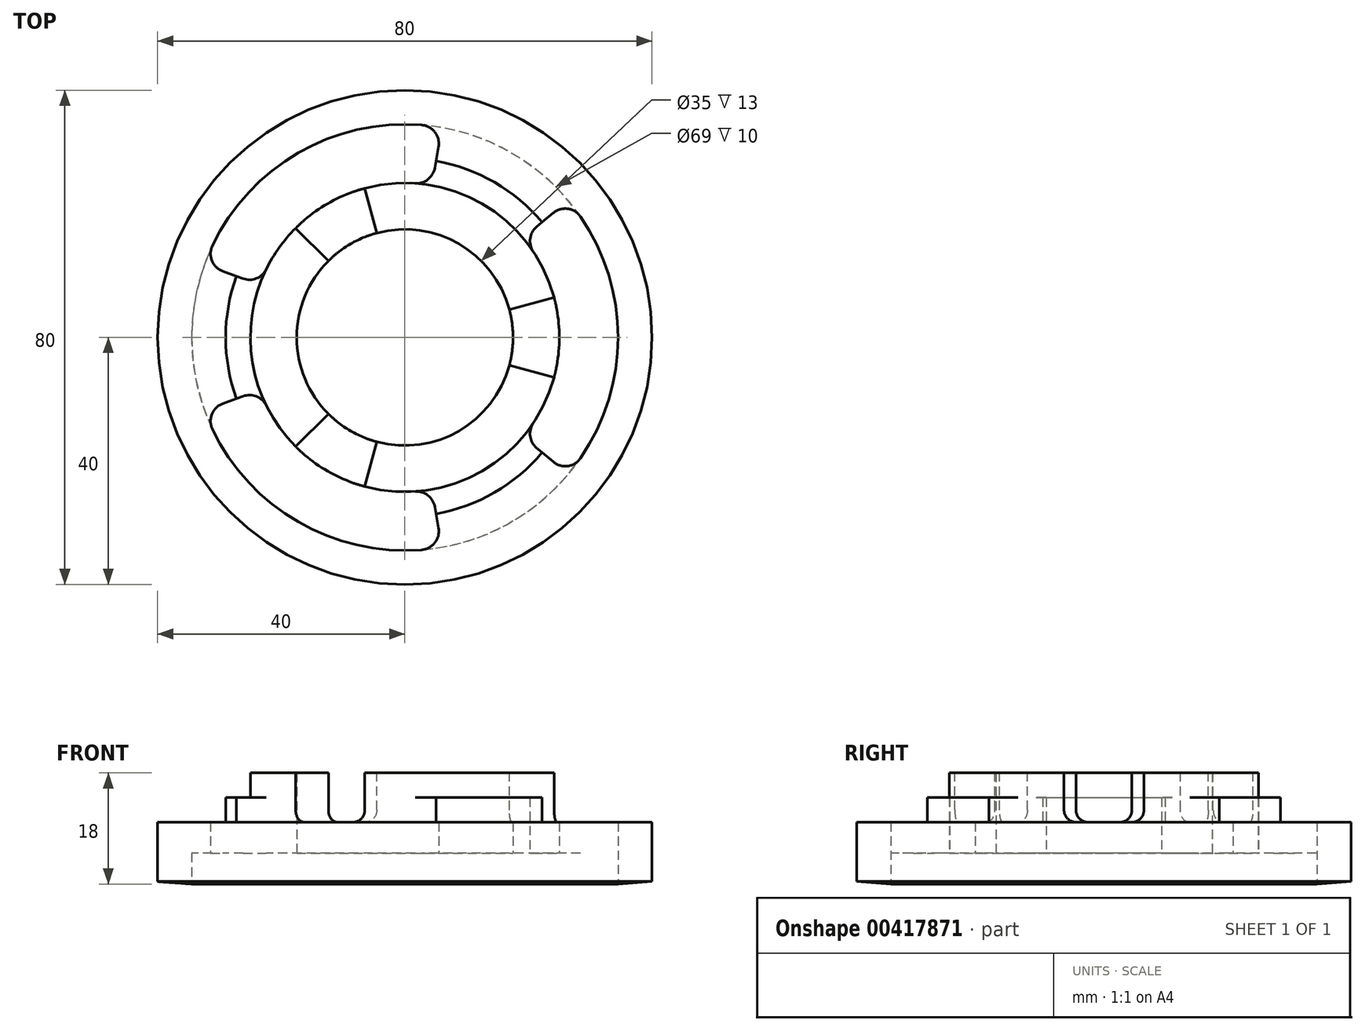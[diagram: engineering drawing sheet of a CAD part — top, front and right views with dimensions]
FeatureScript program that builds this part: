
annotation { "Feature Type Name" : "Feature", "Feature Type Description" : "" }
export const myFeature = defineFeature(function(context is Context, id is Id, definition is map)
    precondition{}
    {
        {
            var Q0;
            Q0=qCreatedBy(makeId("Front.planeOp"),FACE);
            var sketch = newSketch(context, id + "F0", { "sketchPlane" : qUnion([Q0])});
            skLineSegment(sketch, "E0.bottom", {"start": v(-34.5, 3) * mm, "end": v(34.5, 3) * mm});
            skLineSegment(sketch, "E0.left", {"start": v(-34.5, 3) * mm, "end": v(-34.5, -2) * mm});
            skLineSegment(sketch, "E0.right", {"start": v(34.5, 3) * mm, "end": v(34.5, -2) * mm});
            skLineSegment(sketch, "E1", {"start": v(62.5, 0) * mm, "end": v(34.5, -2) * mm});
            skPoint(sketch, "E2.orphan", {"position": v(34.5, 0) * mm});
            skLineSegment(sketch, "E3", {"start": v(-62.5, 0) * mm, "end": v(-34.5, -2) * mm});
            skPoint(sketch, "E4.orphan", {"position": v(0, 3) * mm});
            skLineSegment(sketch, "E5", {"start": v(-34.5, -2) * mm, "end": v(34.5, -2) * mm, "construction": true});
            skLineSegment(sketch, "E6", {"start": v(-40, -1.6) * mm, "end": v(-40, 8) * mm});
            skLineSegment(sketch, "E7", {"start": v(-40, 8) * mm, "end": v(-29, 8) * mm});
            skLineSegment(sketch, "E8", {"start": v(40, 8) * mm, "end": v(40, -1.6) * mm});
            skLineSegment(sketch, "E9", {"start": v(-29, 8) * mm, "end": v(-29, 12) * mm});
            skLineSegment(sketch, "E10", {"start": v(-25, 16) * mm, "end": v(25, 16) * mm});
            skLineSegment(sketch, "E11", {"start": v(29, 12) * mm, "end": v(29, 8) * mm});
            skLineSegment(sketch, "E12.trimOffspring", {"start": v(29, 8) * mm, "end": v(40, 8) * mm});
            skLineSegment(sketch, "E13", {"start": v(17.5, 16) * mm, "end": v(17.5, 3) * mm});
            skLineSegment(sketch, "E14", {"start": v(-17.5, 16) * mm, "end": v(-17.5, 3) * mm});
            skLineSegment(sketch, "E15", {"start": v(0, 0) * mm, "end": v(0, 16) * mm, "construction": true});
            skLineSegment(sketch, "E16", {"start": v(25, 16) * mm, "end": v(25, 12) * mm});
            skLineSegment(sketch, "E17", {"start": v(25, 12) * mm, "end": v(29, 12) * mm});
            skPoint(sketch, "E18.orphan", {"position": v(29, 16) * mm});
            skLineSegment(sketch, "E19.MirrorCS", {"start": v(-25, 12) * mm, "end": v(-29, 12) * mm});
            skLineSegment(sketch, "E20.MirrorCS", {"start": v(-25, 16) * mm, "end": v(-25, 12) * mm});
            skPoint(sketch, "E21.orphan", {"position": v(-29, 16) * mm});
            skSolve(sketch);
        }
        {
            var Q0;
            {var subQ1=sQuery(id+"F0.wireOp",EDGE,"E0.right");Q0=makeQuery(id+"F0.imprint","IMPRINT",FACE,{"disambiguationData":[TD([[makeQuery(id+"F0.imprint","IMPRINT",EDGE,{"derivedFrom":subQ1}),1.0]])]});}
            var Q1;
            {var subQ1=sQuery(id+"F0.wireOp",EDGE,"E11");Q1=makeQuery(id+"F0.imprint","IMPRINT",FACE,{"disambiguationData":[TD([[makeQuery(id+"F0.imprint","IMPRINT",EDGE,{"derivedFrom":subQ1}),-1.0]])]});}
            var Q2;
            Q2=sQuery(id+"F0.wireOp",EDGE,"E15");
            revolve(context, id + "F1", {"surfaceOperationType" : NewSurfaceOperationType.NEW, "entities" : qUnion([Q0, Q1]), "axis" : qUnion([Q2]), "revolveType" : RevolveType.FULL});
        }
        {
            var Q0;
            Q0=makeQuery(id+"F1.opRevolve","SWEPT_FACE",FACE,{"disambiguationData":[OSD([sQuery(id+"F0.wireOp",EDGE,"E0.bottom")])]});
            var sketch = newSketch(context, id + "F2", { "sketchPlane" : qUnion([Q0])});
            skArc(sketch, "E22.0", {"start": v(26.43, -22.18) * mm, "mid": v(34.5, 0) * mm, "end": v(26.43, 22.18) * mm});
            skArc(sketch, "E23", {"start": v(19.15, -16.07) * mm, "mid": v(25, 0) * mm, "end": v(19.15, 16.07) * mm});
            skLineSegment(sketch, "E24", {"start": v(19.15, 16.07) * mm, "end": v(26.43, 22.18) * mm});
            skLineSegment(sketch, "E25", {"start": v(26.43, 22.18) * mm, "end": v(19.15, 16.07) * mm});
            skLineSegment(sketch, "E26", {"start": v(26.43, -22.18) * mm, "end": v(19.15, -16.07) * mm});
            skLineSegment(sketch, "E27.1.0", {"start": v(-23.5, 8.55) * mm, "end": v(-32.42, 11.8) * mm});
            skLineSegment(sketch, "E27.1.1", {"start": v(6, 33.98) * mm, "end": v(4.34, 24.62) * mm});
            skLineSegment(sketch, "E27.2.0", {"start": v(4.34, -24.62) * mm, "end": v(6, -33.98) * mm});
            skLineSegment(sketch, "E27.2.1", {"start": v(-32.42, -11.8) * mm, "end": v(-23.5, -8.55) * mm});
            skArc(sketch, "E28", {"start": v(4.34, 24.62) * mm, "mid": v(-12.5, 21.65) * mm, "end": v(-23.5, 8.55) * mm});
            skArc(sketch, "E29", {"start": v(6, 33.98) * mm, "mid": v(-17.25, 29.88) * mm, "end": v(-32.42, 11.8) * mm});
            skArc(sketch, "E30", {"start": v(-23.5, -8.55) * mm, "mid": v(-12.5, -21.65) * mm, "end": v(4.34, -24.62) * mm});
            skArc(sketch, "E31", {"start": v(-32.42, -11.8) * mm, "mid": v(-17.25, -29.88) * mm, "end": v(6, -33.98) * mm});
            skLineSegment(sketch, "E32", {"start": v(-24.78, -3.5) * mm, "end": v(-17.15, -3.5) * mm});
            skLineSegment(sketch, "E33", {"start": v(-24.85, 3.5) * mm, "end": v(-17.15, 3.5) * mm});
            skSolve(sketch);
        }
        {
            var Q0;
            Q0=makeQuery(id+"F2.imprint","IMPRINT",FACE,{"disambiguationData":[TD([[makeQuery(id+"F2.imprint","IMPRINT",EDGE,{"derivedFrom":sQuery(id+"F2.wireOp",EDGE,"E22.0")}),1.0]])]});
            var Q1;
            Q1=makeQuery(id+"F2.imprint","IMPRINT",FACE,{"disambiguationData":[TD([[makeQuery(id+"F2.imprint","IMPRINT",EDGE,{"derivedFrom":sQuery(id+"F2.wireOp",EDGE,"E27.1.0")}),-1.0]])]});
            var Q2;
            Q2=makeQuery(id+"F2.imprint","IMPRINT",FACE,{"disambiguationData":[TD([[makeQuery(id+"F2.imprint","IMPRINT",EDGE,{"derivedFrom":sQuery(id+"F2.wireOp",EDGE,"E27.2.0")}),-1.0]])]});
            extrude(context, id + "F3", {"entities" : qUnion([Q0, Q1, Q2]), "operationType" : NewBodyOperationType.REMOVE, "endBound" : BoundingType.THROUGH_ALL, "oppositeDirection" : true, "depth" : 25 * mm, "offsetDistance" : 25 * mm});
        }
        {
            var Q0;
            Q0=makeQuery(id+"F3.boolean.opBoolean","COPY",EDGE,{"derivedFrom":makeQuery(id+"F3.opExtrude","SWEPT_EDGE",EDGE,{"disambiguationData":[OSD([sQuery(id+"F0.wireOp",EDGE,"E0.bottom"),sQuery(id+"F0.wireOp",EDGE,"E0.right"),sQuery(id+"F2.wireOp",EDGE,"E27.1.0"),sQuery(id+"F2.wireOp",EDGE,"E29")])]})});
            var Q1;
            Q1=makeQuery(id+"F3.boolean.opBoolean","COPY",EDGE,{"derivedFrom":makeQuery(id+"F3.opExtrude","SWEPT_EDGE",EDGE,{"disambiguationData":[OSD([sQuery(id+"F2.wireOp",EDGE,"E27.1.0"),sQuery(id+"F2.wireOp",EDGE,"E28")])]})});
            var Q2;
            Q2=makeQuery(id+"F3.boolean.opBoolean","COPY",EDGE,{"derivedFrom":makeQuery(id+"F3.opExtrude","SWEPT_EDGE",EDGE,{"disambiguationData":[OSD([sQuery(id+"F2.wireOp",EDGE,"E27.1.1"),sQuery(id+"F2.wireOp",EDGE,"E28")])]})});
            var Q3;
            Q3=makeQuery(id+"F3.boolean.opBoolean","COPY",EDGE,{"derivedFrom":makeQuery(id+"F3.opExtrude","SWEPT_EDGE",EDGE,{"disambiguationData":[OSD([sQuery(id+"F0.wireOp",EDGE,"E0.bottom"),sQuery(id+"F0.wireOp",EDGE,"E0.right"),sQuery(id+"F2.wireOp",EDGE,"E27.1.1"),sQuery(id+"F2.wireOp",EDGE,"E29")])]})});
            var Q4;
            Q4=makeQuery(id+"F3.boolean.opBoolean","COPY",EDGE,{"derivedFrom":makeQuery(id+"F3.opExtrude","SWEPT_EDGE",EDGE,{"disambiguationData":[OSD([sQuery(id+"F2.wireOp",EDGE,"E23"),sQuery(id+"F2.wireOp",EDGE,"E25")])]})});
            var Q5;
            Q5=makeQuery(id+"F3.boolean.opBoolean","COPY",EDGE,{"derivedFrom":makeQuery(id+"F3.opExtrude","SWEPT_EDGE",EDGE,{"disambiguationData":[OSD([sQuery(id+"F0.wireOp",EDGE,"E0.bottom"),sQuery(id+"F0.wireOp",EDGE,"E0.right"),sQuery(id+"F2.wireOp",EDGE,"E22.0"),sQuery(id+"F2.wireOp",EDGE,"E25")])]})});
            var Q6;
            Q6=makeQuery(id+"F3.boolean.opBoolean","COPY",EDGE,{"derivedFrom":makeQuery(id+"F3.opExtrude","SWEPT_EDGE",EDGE,{"disambiguationData":[OSD([sQuery(id+"F0.wireOp",EDGE,"E0.bottom"),sQuery(id+"F0.wireOp",EDGE,"E0.right"),sQuery(id+"F2.wireOp",EDGE,"E22.0"),sQuery(id+"F2.wireOp",EDGE,"E26")])]})});
            var Q7;
            Q7=makeQuery(id+"F3.boolean.opBoolean","COPY",EDGE,{"derivedFrom":makeQuery(id+"F3.opExtrude","SWEPT_EDGE",EDGE,{"disambiguationData":[OSD([sQuery(id+"F2.wireOp",EDGE,"E23"),sQuery(id+"F2.wireOp",EDGE,"E26")])]})});
            var Q8;
            Q8=makeQuery(id+"F3.boolean.opBoolean","COPY",EDGE,{"derivedFrom":makeQuery(id+"F3.opExtrude","SWEPT_EDGE",EDGE,{"disambiguationData":[OSD([sQuery(id+"F2.wireOp",EDGE,"E27.2.0"),sQuery(id+"F2.wireOp",EDGE,"E30")])]})});
            var Q9;
            Q9=makeQuery(id+"F3.boolean.opBoolean","COPY",EDGE,{"derivedFrom":makeQuery(id+"F3.opExtrude","SWEPT_EDGE",EDGE,{"disambiguationData":[OSD([sQuery(id+"F0.wireOp",EDGE,"E0.bottom"),sQuery(id+"F0.wireOp",EDGE,"E0.right"),sQuery(id+"F2.wireOp",EDGE,"E27.2.0"),sQuery(id+"F2.wireOp",EDGE,"E31")])]})});
            var Q10;
            Q10=makeQuery(id+"F3.boolean.opBoolean","COPY",EDGE,{"derivedFrom":makeQuery(id+"F3.opExtrude","SWEPT_EDGE",EDGE,{"disambiguationData":[OSD([sQuery(id+"F0.wireOp",EDGE,"E0.bottom"),sQuery(id+"F0.wireOp",EDGE,"E0.right"),sQuery(id+"F2.wireOp",EDGE,"E27.2.1"),sQuery(id+"F2.wireOp",EDGE,"E31")])]})});
            var Q11;
            Q11=makeQuery(id+"F3.boolean.opBoolean","COPY",EDGE,{"derivedFrom":makeQuery(id+"F3.opExtrude","SWEPT_EDGE",EDGE,{"disambiguationData":[OSD([sQuery(id+"F2.wireOp",EDGE,"E27.2.1"),sQuery(id+"F2.wireOp",EDGE,"E30")])]})});
            fillet(context, id + "F4", {"entities" : qUnion([Q0, Q1, Q2, Q3, Q4, Q5, Q6, Q7, Q8, Q9, Q10, Q11]), "tangentPropagation" : true, "radius" : 3 * mm, "defaultsChanged" : false, "vertexSettings" : [], "allowEdgeOverflow" : false});
        }
        {
            var Q0;
            Q0=makeQuery(id+"F1.opRevolve","SWEPT_FACE",FACE,{"disambiguationData":[OSD([sQuery(id+"F0.wireOp",EDGE,"E10")])]});
            var sketch = newSketch(context, id + "F5", { "sketchPlane" : qUnion([Q0])});
            skLineSegment(sketch, "E34", {"start": v(16.9, 4.53) * mm, "end": v(24.15, 6.47) * mm});
            skLineSegment(sketch, "E35", {"start": v(16.9, -4.53) * mm, "end": v(24.15, -6.47) * mm});
            skArc(sketch, "E36", {"start": v(16.9, 4.53) * mm, "mid": v(17.5, 0) * mm, "end": v(16.9, -4.53) * mm});
            skArc(sketch, "E37", {"start": v(24.15, 6.47) * mm, "mid": v(25, 0) * mm, "end": v(24.15, -6.47) * mm});
            skLineSegment(sketch, "E38.1.0", {"start": v(-12.37, 12.37) * mm, "end": v(-17.68, 17.68) * mm});
            skArc(sketch, "E38.1.1", {"start": v(-12.37, 12.37) * mm, "mid": v(-8.75, 15.16) * mm, "end": v(-4.53, 16.9) * mm});
            skArc(sketch, "E38.1.2", {"start": v(-17.68, 17.68) * mm, "mid": v(-12.5, 21.65) * mm, "end": v(-6.47, 24.15) * mm});
            skLineSegment(sketch, "E38.1.3", {"start": v(-4.53, 16.9) * mm, "end": v(-6.47, 24.15) * mm});
            skLineSegment(sketch, "E38.2.0", {"start": v(-4.53, -16.9) * mm, "end": v(-6.47, -24.15) * mm});
            skArc(sketch, "E38.2.1", {"start": v(-4.53, -16.9) * mm, "mid": v(-8.75, -15.16) * mm, "end": v(-12.37, -12.37) * mm});
            skArc(sketch, "E38.2.2", {"start": v(-6.47, -24.15) * mm, "mid": v(-12.5, -21.65) * mm, "end": v(-17.68, -17.68) * mm});
            skLineSegment(sketch, "E38.2.3", {"start": v(-12.37, -12.37) * mm, "end": v(-17.68, -17.68) * mm});
            skSolve(sketch);
        }
        {
            var Q0;
            Q0=makeQuery(id+"F5.imprint","IMPRINT",FACE,{"disambiguationData":[TD([[makeQuery(id+"F5.imprint","IMPRINT",EDGE,{"derivedFrom":sQuery(id+"F5.wireOp",EDGE,"E38.1.0")}),-1.0]])]});
            var Q1;
            Q1=makeQuery(id+"F5.imprint","IMPRINT",FACE,{"disambiguationData":[TD([[makeQuery(id+"F5.imprint","IMPRINT",EDGE,{"derivedFrom":sQuery(id+"F5.wireOp",EDGE,"E34")}),-1.0]])]});
            var Q2;
            Q2=makeQuery(id+"F5.imprint","IMPRINT",FACE,{"disambiguationData":[TD([[makeQuery(id+"F5.imprint","IMPRINT",EDGE,{"derivedFrom":sQuery(id+"F5.wireOp",EDGE,"E38.2.0")}),-1.0]])]});
            extrude(context, id + "F6", {"entities" : qUnion([Q0, Q1, Q2]), "operationType" : NewBodyOperationType.REMOVE, "oppositeDirection" : true, "depth" : 8 * mm, "offsetDistance" : 25 * mm});
        }
        {
            var Q0;
            Q0=makeQuery(id+"F6.boolean.opBoolean","COPY",EDGE,{"derivedFrom":makeQuery(id+"F6.opExtrude","CAP_EDGE",EDGE,{"disambiguationData":[OSD([sQuery(id+"F5.wireOp",EDGE,"E38.1.3")])],"isStart":true})});
            var Q1;
            Q1=makeQuery(id+"F6.boolean.opBoolean","COPY",EDGE,{"derivedFrom":makeQuery(id+"F6.opExtrude","CAP_EDGE",EDGE,{"disambiguationData":[OSD([sQuery(id+"F5.wireOp",EDGE,"E34")])],"isStart":true})});
            var Q2;
            Q2=makeQuery(id+"F6.boolean.opBoolean","COPY",EDGE,{"derivedFrom":makeQuery(id+"F6.opExtrude","CAP_EDGE",EDGE,{"disambiguationData":[OSD([sQuery(id+"F5.wireOp",EDGE,"E35")])],"isStart":true})});
            var Q3;
            Q3=makeQuery(id+"F6.boolean.opBoolean","COPY",EDGE,{"derivedFrom":makeQuery(id+"F6.opExtrude","CAP_EDGE",EDGE,{"disambiguationData":[OSD([sQuery(id+"F5.wireOp",EDGE,"E38.2.0")])],"isStart":true})});
            var Q4;
            Q4=makeQuery(id+"F6.boolean.opBoolean","COPY",EDGE,{"derivedFrom":makeQuery(id+"F6.opExtrude","CAP_EDGE",EDGE,{"disambiguationData":[OSD([sQuery(id+"F5.wireOp",EDGE,"E38.2.3")])],"isStart":true})});
            var Q5;
            Q5=makeQuery(id+"F6.boolean.opBoolean","COPY",EDGE,{"derivedFrom":makeQuery(id+"F6.opExtrude","CAP_EDGE",EDGE,{"disambiguationData":[OSD([sQuery(id+"F5.wireOp",EDGE,"E38.1.3")])],"isStart":false})});
            var Q6;
            Q6=makeQuery(id+"F6.boolean.opBoolean","COPY",EDGE,{"derivedFrom":makeQuery(id+"F6.opExtrude","CAP_EDGE",EDGE,{"disambiguationData":[OSD([sQuery(id+"F5.wireOp",EDGE,"E38.1.0")])],"isStart":false})});
            var Q7;
            Q7=makeQuery(id+"F6.boolean.opBoolean","COPY",EDGE,{"derivedFrom":makeQuery(id+"F6.opExtrude","CAP_EDGE",EDGE,{"disambiguationData":[OSD([sQuery(id+"F5.wireOp",EDGE,"E38.1.0")])],"isStart":true})});
            var Q8;
            Q8=makeQuery(id+"F6.boolean.opBoolean","COPY",EDGE,{"derivedFrom":makeQuery(id+"F6.opExtrude","CAP_EDGE",EDGE,{"disambiguationData":[OSD([sQuery(id+"F5.wireOp",EDGE,"E38.2.0")])],"isStart":false})});
            var Q9;
            Q9=makeQuery(id+"F6.boolean.opBoolean","COPY",EDGE,{"derivedFrom":makeQuery(id+"F6.opExtrude","CAP_EDGE",EDGE,{"disambiguationData":[OSD([sQuery(id+"F5.wireOp",EDGE,"E38.2.3")])],"isStart":false})});
            var Q10;
            Q10=makeQuery(id+"F6.boolean.opBoolean","COPY",EDGE,{"derivedFrom":makeQuery(id+"F6.opExtrude","CAP_EDGE",EDGE,{"disambiguationData":[OSD([sQuery(id+"F5.wireOp",EDGE,"E35")])],"isStart":false})});
            var Q11;
            Q11=makeQuery(id+"F6.boolean.opBoolean","COPY",EDGE,{"derivedFrom":makeQuery(id+"F6.opExtrude","CAP_EDGE",EDGE,{"disambiguationData":[OSD([sQuery(id+"F5.wireOp",EDGE,"E34")])],"isStart":false})});
            fillet(context, id + "F7", {"entities" : qUnion([Q0, Q1, Q2, Q3, Q4, Q5, Q6, Q7, Q8, Q9, Q10, Q11]), "tangentPropagation" : true, "radius" : 2 * mm, "defaultsChanged" : false, "vertexSettings" : [], "allowEdgeOverflow" : false});
        }
    });
